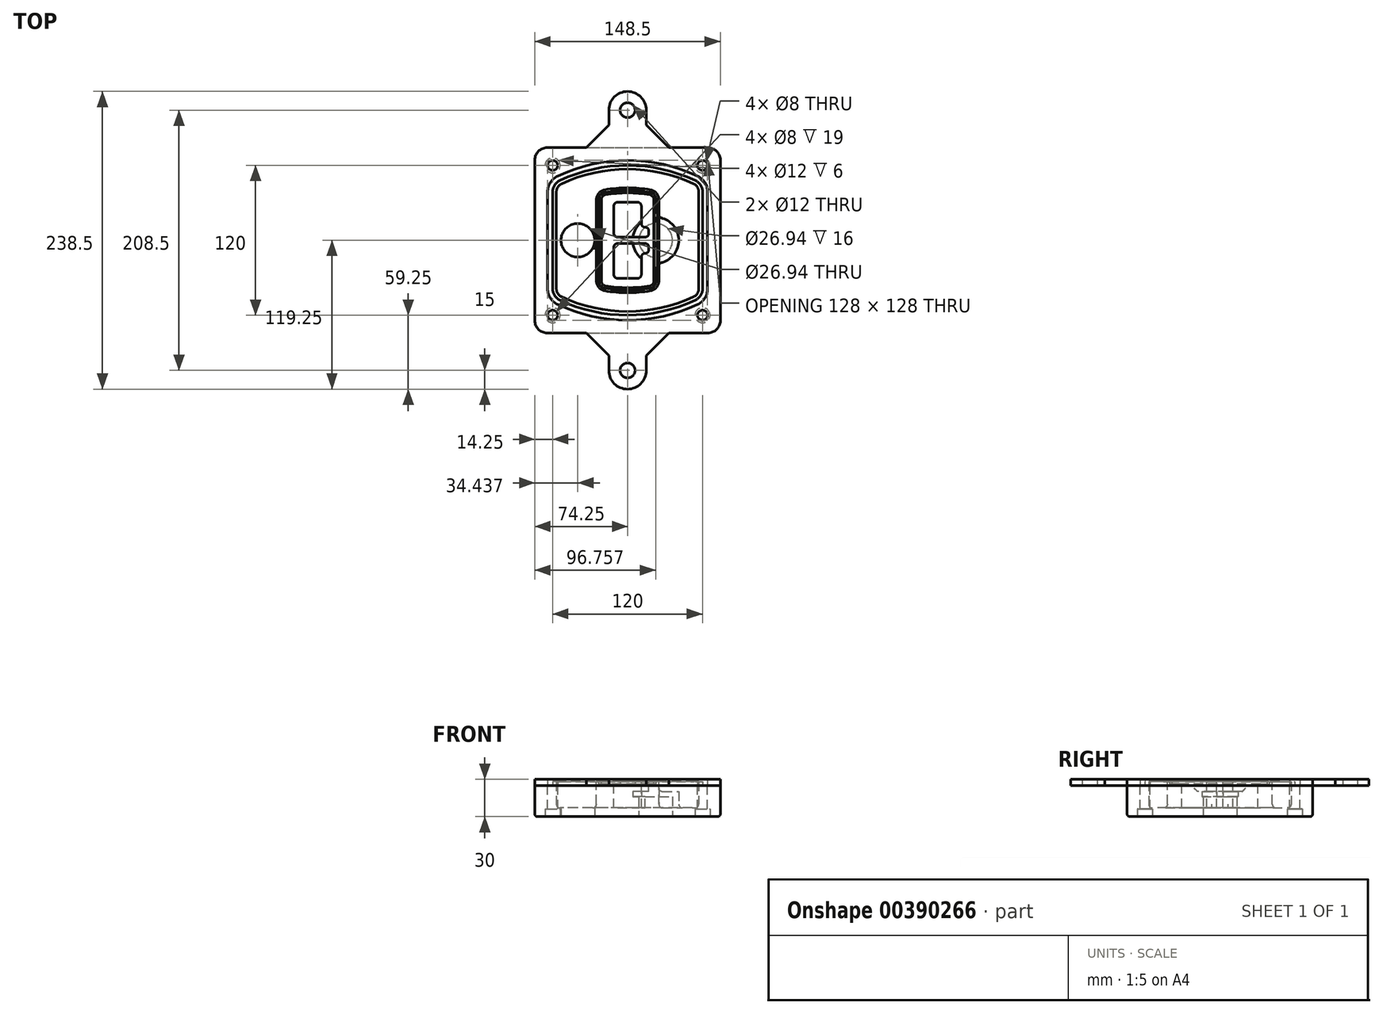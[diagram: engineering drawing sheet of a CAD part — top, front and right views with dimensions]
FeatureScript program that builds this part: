
annotation { "Feature Type Name" : "Feature", "Feature Type Description" : "" }
export const myFeature = defineFeature(function(context is Context, id is Id, definition is map)
    precondition{}
    {
        {
            var Q0;
            Q0=qCreatedBy(makeId("Top.planeOp"),FACE);
            var sketch = newSketch(context, id + "F0", { "sketchPlane" : qUnion([Q0])});
            skPoint(sketch, "E0.rect.middle", {"position": v(0, 0) * mm});
            skLineSegment(sketch, "E1.bottom", {"start": v(-64.25, -74.25) * mm, "end": v(64.25, -74.25) * mm});
            skLineSegment(sketch, "E1.top", {"start": v(-64.25, 74.25) * mm, "end": v(64.25, 74.25) * mm});
            skLineSegment(sketch, "E1.left", {"start": v(-74.25, -64.25) * mm, "end": v(-74.25, 64.25) * mm});
            skLineSegment(sketch, "E1.right", {"start": v(74.25, -64.25) * mm, "end": v(74.25, 64.25) * mm});
            skLineSegment(sketch, "E2", {"start": v(-74.25, 74.25) * mm, "end": v(74.25, -74.25) * mm, "construction": true});
            skLineSegment(sketch, "E3", {"start": v(74.25, 74.25) * mm, "end": v(-74.25, -74.25) * mm, "construction": true});
            skCircle(sketch, "E4", {"center": v(-60, 60) * mm, "radius": 4 * mm});
            skCircle(sketch, "E5", {"center": v(60, 60) * mm, "radius": 4 * mm});
            skCircle(sketch, "E6", {"center": v(60, -60) * mm, "radius": 4 * mm});
            skCircle(sketch, "E7", {"center": v(-60, -60) * mm, "radius": 4 * mm});
            skLineSegment(sketch, "E8", {"start": v(-60, 60) * mm, "end": v(60, 60) * mm, "construction": true});
            skLineSegment(sketch, "E9", {"start": v(60, 60) * mm, "end": v(60, -60) * mm, "construction": true});
            skLineSegment(sketch, "E10", {"start": v(60, -60) * mm, "end": v(-60, -60) * mm, "construction": true});
            skLineSegment(sketch, "E11", {"start": v(-60, -60) * mm, "end": v(-60, 60) * mm, "construction": true});
            skLineSegment(sketch, "E12", {"start": v(-60, 38.83) * mm, "end": v(-60, -38.83) * mm});
            skLineSegment(sketch, "E13", {"start": v(60, 38.83) * mm, "end": v(60, -38.83) * mm});
            skArc(sketch, "E14", {"start": v(54.26, 47.88) * mm, "mid": v(0, 60) * mm, "end": v(-54.26, 47.88) * mm});
            skArc(sketch, "E15", {"start": v(-54.26, -47.88) * mm, "mid": v(0, -60) * mm, "end": v(54.26, -47.88) * mm});
            skLineSegment(sketch, "E16", {"start": v(-60, 0) * mm, "end": v(60, 0) * mm, "construction": true});
            skPoint(sketch, "E17.visualSharp", {"position": v(-60, -45) * mm});
            skArc(sketch, "E17.filletArc", {"start": v(-60, -38.83) * mm, "mid": v(-58.44, -44.2) * mm, "end": v(-54.26, -47.88) * mm});
            skPoint(sketch, "E18.visualSharp", {"position": v(-60, 45) * mm});
            skArc(sketch, "E18.filletArc", {"start": v(-54.26, 47.88) * mm, "mid": v(-58.44, 44.2) * mm, "end": v(-60, 38.83) * mm});
            skPoint(sketch, "E19.visualSharp", {"position": v(60, 45) * mm});
            skArc(sketch, "E19.filletArc", {"start": v(60, 38.83) * mm, "mid": v(58.44, 44.2) * mm, "end": v(54.26, 47.88) * mm});
            skPoint(sketch, "E20.visualSharp", {"position": v(60, -45) * mm});
            skArc(sketch, "E20.filletArc", {"start": v(54.26, -47.88) * mm, "mid": v(58.44, -44.2) * mm, "end": v(60, -38.83) * mm});
            skPoint(sketch, "E21.visualSharp", {"position": v(-74.25, 74.25) * mm});
            skArc(sketch, "E21.filletArc", {"start": v(-64.25, 74.25) * mm, "mid": v(-71.32, 71.32) * mm, "end": v(-74.25, 64.25) * mm});
            skPoint(sketch, "E22.visualSharp", {"position": v(74.25, 74.25) * mm});
            skArc(sketch, "E22.filletArc", {"start": v(74.25, 64.25) * mm, "mid": v(71.32, 71.32) * mm, "end": v(64.25, 74.25) * mm});
            skPoint(sketch, "E23.visualSharp", {"position": v(74.25, -74.25) * mm});
            skArc(sketch, "E23.filletArc", {"start": v(64.25, -74.25) * mm, "mid": v(71.32, -71.32) * mm, "end": v(74.25, -64.25) * mm});
            skPoint(sketch, "E24.visualSharp", {"position": v(-74.25, -74.25) * mm});
            skArc(sketch, "E24.filletArc", {"start": v(-74.25, -64.25) * mm, "mid": v(-71.32, -71.32) * mm, "end": v(-64.25, -74.25) * mm});
            skArc(sketch, "E25.0", {"start": v(57, 38.83) * mm, "mid": v(55.9, 42.58) * mm, "end": v(52.98, 45.17) * mm});
            skLineSegment(sketch, "E25.1", {"start": v(57, 38.83) * mm, "end": v(57, -38.83) * mm});
            skArc(sketch, "E25.2", {"start": v(52.98, -45.17) * mm, "mid": v(55.9, -42.58) * mm, "end": v(57, -38.83) * mm});
            skArc(sketch, "E25.3", {"start": v(-52.98, -45.17) * mm, "mid": v(0, -57) * mm, "end": v(52.98, -45.17) * mm});
            skArc(sketch, "E25.4", {"start": v(-57, -38.83) * mm, "mid": v(-55.9, -42.58) * mm, "end": v(-52.98, -45.17) * mm});
            skArc(sketch, "E25.5", {"start": v(52.98, 45.17) * mm, "mid": v(0, 57) * mm, "end": v(-52.98, 45.17) * mm});
            skLineSegment(sketch, "E25.6", {"start": v(-57, 38.83) * mm, "end": v(-57, -38.83) * mm});
            skArc(sketch, "E25.7", {"start": v(-52.98, 45.17) * mm, "mid": v(-55.9, 42.58) * mm, "end": v(-57, 38.83) * mm});
            skArc(sketch, "E26.0", {"start": v(-55.96, 51.5) * mm, "mid": v(-61.82, 46.33) * mm, "end": v(-64, 38.83) * mm});
            skArc(sketch, "E26.1", {"start": v(55.96, 51.5) * mm, "mid": v(0, 64) * mm, "end": v(-55.96, 51.5) * mm});
            skArc(sketch, "E26.2", {"start": v(64, 38.83) * mm, "mid": v(61.82, 46.33) * mm, "end": v(55.96, 51.5) * mm});
            skLineSegment(sketch, "E26.3", {"start": v(64, 38.83) * mm, "end": v(64, -38.83) * mm});
            skArc(sketch, "E26.4", {"start": v(55.96, -51.5) * mm, "mid": v(61.82, -46.33) * mm, "end": v(64, -38.83) * mm});
            skLineSegment(sketch, "E26.5", {"start": v(-64, 38.83) * mm, "end": v(-64, -38.83) * mm});
            skArc(sketch, "E26.6", {"start": v(-55.96, -51.5) * mm, "mid": v(0, -64) * mm, "end": v(55.96, -51.5) * mm});
            skArc(sketch, "E26.7", {"start": v(-64, -38.83) * mm, "mid": v(-61.82, -46.33) * mm, "end": v(-55.96, -51.5) * mm});
            skCircle(sketch, "E27", {"center": v(0, 104.25) * mm, "radius": 6 * mm});
            skArc(sketch, "E28", {"start": v(15, 104.25) * mm, "mid": v(0, 119.25) * mm, "end": v(-15, 104.25) * mm});
            skLineSegment(sketch, "E29", {"start": v(-15, 104.25) * mm, "end": v(-15, 92.25) * mm});
            skLineSegment(sketch, "E30", {"start": v(15, 104.25) * mm, "end": v(15, 92.25) * mm});
            skLineSegment(sketch, "E31", {"start": v(15, 92.25) * mm, "end": v(33, 74.25) * mm});
            skLineSegment(sketch, "E32", {"start": v(-15, 92.25) * mm, "end": v(-33, 74.25) * mm});
            skLineSegment(sketch, "E33.MirrorCS", {"start": v(-15, -92.25) * mm, "end": v(-33, -74.25) * mm});
            skLineSegment(sketch, "E34.MirrorCS", {"start": v(-15, -104.25) * mm, "end": v(-15, -92.25) * mm});
            skArc(sketch, "E35.MirrorCS", {"start": v(15, -104.25) * mm, "mid": v(0, -119.25) * mm, "end": v(-15, -104.25) * mm});
            skCircle(sketch, "E36.MirrorC", {"center": v(0, -104.25) * mm, "radius": 6 * mm});
            skLineSegment(sketch, "E37.MirrorCS", {"start": v(15, -104.25) * mm, "end": v(15, -92.25) * mm});
            skLineSegment(sketch, "E38.MirrorCS", {"start": v(15, -92.25) * mm, "end": v(33, -74.25) * mm});
            skSolve(sketch);
        }
        {
            var Q0;
            Q0=makeQuery(id+"F0.imprint","IMPRINT",FACE,{"disambiguationData":[TD([[makeQuery(id+"F0.imprint","IMPRINT",EDGE,{"derivedFrom":sQuery(id+"F0.wireOp",EDGE,"E1.bottom")}),1.0]])]});
            var Q1;
            Q1=makeQuery(id+"F0.imprint","IMPRINT",FACE,{"disambiguationData":[TD([[makeQuery(id+"F0.imprint","IMPRINT",EDGE,{"derivedFrom":sQuery(id+"F0.wireOp",EDGE,"E12")}),1.0]])]});
            var Q2;
            Q2=makeQuery(id+"F0.imprint","IMPRINT",FACE,{"disambiguationData":[TD([[makeQuery(id+"F0.imprint","IMPRINT",EDGE,{"derivedFrom":sQuery(id+"F0.wireOp",EDGE,"E25.0")}),1.0]])]});
            var Q3;
            Q3=makeQuery(id+"F0.imprint","IMPRINT",FACE,{"disambiguationData":[TD([[makeQuery(id+"F0.imprint","IMPRINT",EDGE,{"derivedFrom":sQuery(id+"F0.wireOp",EDGE,"E12")}),-1.0]])]});
            extrude(context, id + "F1", {"entities" : qUnion([Q0, Q1, Q2, Q3]), "oppositeDirection" : true, "depth" : 25 * mm});
        }
        {
            var Q0;
            Q0=makeQuery(id+"F0.imprint","IMPRINT",FACE,{"disambiguationData":[TD([[makeQuery(id+"F0.imprint","IMPRINT",EDGE,{"derivedFrom":sQuery(id+"F0.wireOp",EDGE,"E12")}),1.0]])]});
            extrude(context, id + "F2", {"entities" : qUnion([Q0]), "operationType" : NewBodyOperationType.ADD, "depth" : 3 * mm});
        }
        {
            var Q0;
            Q0=makeQuery(id+"F0.imprint","IMPRINT",FACE,{"disambiguationData":[TD([[makeQuery(id+"F0.imprint","IMPRINT",EDGE,{"derivedFrom":sQuery(id+"F0.wireOp",EDGE,"E25.0")}),1.0]])]});
            extrude(context, id + "F3", {"entities" : qUnion([Q0]), "operationType" : NewBodyOperationType.REMOVE, "oppositeDirection" : true, "depth" : 18 * mm});
        }
        {
            var Q0;
            Q0=makeQuery(id+"F2.opExtrude","CAP_FACE",FACE,{"disambiguationData":[OSD([sQuery(id+"F0.wireOp",EDGE,"E12"),sQuery(id+"F0.wireOp",EDGE,"E13"),sQuery(id+"F0.wireOp",EDGE,"E14"),sQuery(id+"F0.wireOp",EDGE,"E15"),sQuery(id+"F0.wireOp",EDGE,"E17.filletArc"),sQuery(id+"F0.wireOp",EDGE,"E18.filletArc"),sQuery(id+"F0.wireOp",EDGE,"E19.filletArc"),sQuery(id+"F0.wireOp",EDGE,"E20.filletArc"),sQuery(id+"F0.wireOp",EDGE,"E25.0"),sQuery(id+"F0.wireOp",EDGE,"E25.1"),sQuery(id+"F0.wireOp",EDGE,"E25.2"),sQuery(id+"F0.wireOp",EDGE,"E25.3"),sQuery(id+"F0.wireOp",EDGE,"E25.4"),sQuery(id+"F0.wireOp",EDGE,"E25.5"),sQuery(id+"F0.wireOp",EDGE,"E25.6"),sQuery(id+"F0.wireOp",EDGE,"E25.7")])],"isStart":false});
            var sketch = newSketch(context, id + "F4", { "sketchPlane" : qUnion([Q0])});
            skArc(sketch, "E39.0", {"start": v(-18.34, -40.45) * mm, "mid": v(0, -42) * mm, "end": v(18.34, -40.45) * mm});
            skArc(sketch, "E40.0", {"start": v(18.34, 40.45) * mm, "mid": v(0, 42) * mm, "end": v(-18.34, 40.45) * mm});
            skLineSegment(sketch, "E41", {"start": v(-25, 32.57) * mm, "end": v(-25, -32.57) * mm});
            skLineSegment(sketch, "E42", {"start": v(25, 32.57) * mm, "end": v(25, -32.57) * mm});
            skLineSegment(sketch, "E43", {"start": v(-25, 39.1) * mm, "end": v(25, 39.1) * mm, "construction": true});
            skLineSegment(sketch, "E44", {"start": v(-25, -39.1) * mm, "end": v(25, -39.1) * mm, "construction": true});
            skPoint(sketch, "E45.visualSharp", {"position": v(-25, 39.1) * mm});
            skArc(sketch, "E45.filletArc", {"start": v(-18.34, 40.45) * mm, "mid": v(-23.11, 37.73) * mm, "end": v(-25, 32.57) * mm});
            skPoint(sketch, "E46.visualSharp", {"position": v(25, 39.1) * mm});
            skArc(sketch, "E46.filletArc", {"start": v(25, 32.57) * mm, "mid": v(23.11, 37.73) * mm, "end": v(18.34, 40.45) * mm});
            skPoint(sketch, "E47.visualSharp", {"position": v(25, -39.1) * mm});
            skArc(sketch, "E47.filletArc", {"start": v(18.34, -40.45) * mm, "mid": v(23.11, -37.73) * mm, "end": v(25, -32.57) * mm});
            skPoint(sketch, "E48.visualSharp", {"position": v(-25, -39.1) * mm});
            skArc(sketch, "E48.filletArc", {"start": v(-25, -32.57) * mm, "mid": v(-23.11, -37.73) * mm, "end": v(-18.34, -40.45) * mm});
            skArc(sketch, "E49.0", {"start": v(52.98, 45.17) * mm, "mid": v(0, 57) * mm, "end": v(-52.98, 45.17) * mm});
            skArc(sketch, "E49.1", {"start": v(-52.98, 45.17) * mm, "mid": v(-55.9, 42.58) * mm, "end": v(-57, 38.83) * mm});
            skLineSegment(sketch, "E49.2", {"start": v(-57, 38.83) * mm, "end": v(-57, -38.83) * mm});
            skArc(sketch, "E49.3", {"start": v(-57, -38.83) * mm, "mid": v(-55.9, -42.58) * mm, "end": v(-52.98, -45.17) * mm});
            skArc(sketch, "E49.4", {"start": v(-52.98, -45.17) * mm, "mid": v(0, -57) * mm, "end": v(52.98, -45.17) * mm});
            skArc(sketch, "E49.5", {"start": v(52.98, -45.17) * mm, "mid": v(55.9, -42.58) * mm, "end": v(57, -38.83) * mm});
            skLineSegment(sketch, "E49.6", {"start": v(57, 38.83) * mm, "end": v(57, -38.83) * mm});
            skArc(sketch, "E49.7", {"start": v(57, 38.83) * mm, "mid": v(55.9, 42.58) * mm, "end": v(52.98, 45.17) * mm});
            skLineSegment(sketch, "E50.0", {"start": v(23, 32.57) * mm, "end": v(23, -32.57) * mm});
            skArc(sketch, "E50.1", {"start": v(18, -38.48) * mm, "mid": v(21.58, -36.44) * mm, "end": v(23, -32.57) * mm});
            skArc(sketch, "E50.2", {"start": v(-18, -38.48) * mm, "mid": v(0, -40) * mm, "end": v(18, -38.48) * mm});
            skArc(sketch, "E50.3", {"start": v(-23, -32.57) * mm, "mid": v(-21.58, -36.44) * mm, "end": v(-18, -38.48) * mm});
            skLineSegment(sketch, "E50.4", {"start": v(-23, 32.57) * mm, "end": v(-23, -32.57) * mm});
            skArc(sketch, "E50.5", {"start": v(23, 32.57) * mm, "mid": v(21.58, 36.44) * mm, "end": v(18, 38.48) * mm});
            skArc(sketch, "E50.6", {"start": v(-18, 38.48) * mm, "mid": v(-21.58, 36.44) * mm, "end": v(-23, 32.57) * mm});
            skArc(sketch, "E50.7", {"start": v(18, 38.48) * mm, "mid": v(0, 40) * mm, "end": v(-18, 38.48) * mm});
            skArc(sketch, "E51.0", {"start": v(21, 32.57) * mm, "mid": v(20.06, 35.15) * mm, "end": v(17.67, 36.5) * mm});
            skLineSegment(sketch, "E51.1", {"start": v(21, 32.57) * mm, "end": v(21, -32.57) * mm});
            skArc(sketch, "E51.2", {"start": v(17.67, -36.5) * mm, "mid": v(20.06, -35.15) * mm, "end": v(21, -32.57) * mm});
            skArc(sketch, "E51.3", {"start": v(-17.67, -36.5) * mm, "mid": v(0, -38) * mm, "end": v(17.67, -36.5) * mm});
            skArc(sketch, "E51.4", {"start": v(-21, -32.57) * mm, "mid": v(-20.06, -35.15) * mm, "end": v(-17.67, -36.5) * mm});
            skArc(sketch, "E51.5", {"start": v(17.67, 36.5) * mm, "mid": v(0, 38) * mm, "end": v(-17.67, 36.5) * mm});
            skLineSegment(sketch, "E51.6", {"start": v(-21, 32.57) * mm, "end": v(-21, -32.57) * mm});
            skArc(sketch, "E51.7", {"start": v(-17.67, 36.5) * mm, "mid": v(-20.06, 35.15) * mm, "end": v(-21, 32.57) * mm});
            skLineSegment(sketch, "E52", {"start": v(-25, 0) * mm, "end": v(25, 0) * mm, "construction": true});
            skLineSegment(sketch, "E53", {"start": v(-11, 5.5) * mm, "end": v(-11, 27.5) * mm});
            skLineSegment(sketch, "E54", {"start": v(-8, 30.5) * mm, "end": v(8, 30.5) * mm});
            skLineSegment(sketch, "E55", {"start": v(11, 27.5) * mm, "end": v(11, 13.5) * mm});
            skLineSegment(sketch, "E56", {"start": v(14, 10.5) * mm, "end": v(14, 10.5) * mm});
            skLineSegment(sketch, "E57", {"start": v(17, 7.5) * mm, "end": v(17, 5.5) * mm});
            skLineSegment(sketch, "E58", {"start": v(14, 2.5) * mm, "end": v(-8, 2.5) * mm});
            skPoint(sketch, "E59.visualSharp", {"position": v(-11, 30.5) * mm});
            skArc(sketch, "E59.filletArc", {"start": v(-8, 30.5) * mm, "mid": v(-10.12, 29.62) * mm, "end": v(-11, 27.5) * mm});
            skPoint(sketch, "E60.visualSharp", {"position": v(11, 30.5) * mm});
            skArc(sketch, "E60.filletArc", {"start": v(11, 27.5) * mm, "mid": v(10.12, 29.62) * mm, "end": v(8, 30.5) * mm});
            skPoint(sketch, "E61.visualSharp", {"position": v(11, 10.5) * mm});
            skArc(sketch, "E61.filletArc", {"start": v(11, 13.5) * mm, "mid": v(11.88, 11.38) * mm, "end": v(14, 10.5) * mm});
            skPoint(sketch, "E62.visualSharp", {"position": v(17, 10.5) * mm});
            skArc(sketch, "E62.filletArc", {"start": v(17, 7.5) * mm, "mid": v(16.12, 9.62) * mm, "end": v(14, 10.5) * mm});
            skPoint(sketch, "E63.visualSharp", {"position": v(17, 2.5) * mm});
            skArc(sketch, "E63.filletArc", {"start": v(14, 2.5) * mm, "mid": v(16.12, 3.38) * mm, "end": v(17, 5.5) * mm});
            skPoint(sketch, "E64.visualSharp", {"position": v(-11, 2.5) * mm});
            skArc(sketch, "E64.filletArc", {"start": v(-11, 5.5) * mm, "mid": v(-10.12, 3.38) * mm, "end": v(-8, 2.5) * mm});
            skLineSegment(sketch, "E65.0.MirrorCS", {"start": v(14, -2.5) * mm, "end": v(-8, -2.5) * mm});
            skArc(sketch, "E66.0.MirrorCS", {"start": v(-11, -5.5) * mm, "mid": v(-10.12, -3.38) * mm, "end": v(-8, -2.5) * mm});
            skLineSegment(sketch, "E67.0.MirrorCS", {"start": v(-11, -5.5) * mm, "end": v(-11, -27.5) * mm});
            skArc(sketch, "E68.0.MirrorCS", {"start": v(-8, -30.5) * mm, "mid": v(-10.12, -29.62) * mm, "end": v(-11, -27.5) * mm});
            skLineSegment(sketch, "E69.0.MirrorCS", {"start": v(-8, -30.5) * mm, "end": v(8, -30.5) * mm});
            skArc(sketch, "E70.0.MirrorCS", {"start": v(11, -27.5) * mm, "mid": v(10.12, -29.62) * mm, "end": v(8, -30.5) * mm});
            skLineSegment(sketch, "E71.0.MirrorCS", {"start": v(11, -27.5) * mm, "end": v(11, -13.5) * mm});
            skArc(sketch, "E72.0.MirrorCS", {"start": v(11, -13.5) * mm, "mid": v(11.88, -11.38) * mm, "end": v(14, -10.5) * mm});
            skArc(sketch, "E73.0.MirrorCS", {"start": v(17, -7.5) * mm, "mid": v(16.12, -9.62) * mm, "end": v(14, -10.5) * mm});
            skLineSegment(sketch, "E74.0.MirrorCS", {"start": v(17, -7.5) * mm, "end": v(17, -5.5) * mm});
            skArc(sketch, "E75.0.MirrorCS", {"start": v(14, -2.5) * mm, "mid": v(16.12, -3.38) * mm, "end": v(17, -5.5) * mm});
            skSolve(sketch);
        }
        {
            var Q0;
            Q0=makeQuery(id+"F4.imprint","IMPRINT",FACE,{"disambiguationData":[TD([[makeQuery(id+"F4.imprint","IMPRINT",EDGE,{"derivedFrom":sQuery(id+"F4.wireOp",EDGE,"E39.0")}),1.0]])]});
            var Q1;
            Q1=makeQuery(id+"F4.imprint","IMPRINT",FACE,{"disambiguationData":[TD([[makeQuery(id+"F4.imprint","IMPRINT",EDGE,{"derivedFrom":sQuery(id+"F4.wireOp",EDGE,"E50.0")}),-1.0]])]});
            var Q2;
            Q2=makeQuery(id+"F4.imprint","IMPRINT",FACE,{"disambiguationData":[TD([[makeQuery(id+"F4.imprint","IMPRINT",EDGE,{"derivedFrom":sQuery(id+"F4.wireOp",EDGE,"E51.0")}),1.0]])]});
            extrude(context, id + "F5", {"entities" : qUnion([Q0, Q1, Q2]), "operationType" : NewBodyOperationType.ADD, "endBound" : BoundingType.UP_TO_NEXT, "oppositeDirection" : true, "depth" : 25 * mm});
        }
        {
            var Q0;
            Q0=makeQuery(id+"F4.imprint","IMPRINT",FACE,{"disambiguationData":[TD([[makeQuery(id+"F4.imprint","IMPRINT",EDGE,{"derivedFrom":sQuery(id+"F4.wireOp",EDGE,"E50.0")}),-1.0]])]});
            extrude(context, id + "F6", {"entities" : qUnion([Q0]), "operationType" : NewBodyOperationType.REMOVE, "oppositeDirection" : true, "depth" : 2 * mm});
        }
        {
            var Q0;
            Q0=makeQuery(id+"F1.opExtrude","CAP_FACE",FACE,{"disambiguationData":[OSD([sQuery(id+"F0.wireOp",EDGE,"E1.bottom"),sQuery(id+"F0.wireOp",EDGE,"E1.top"),sQuery(id+"F0.wireOp",EDGE,"E1.left"),sQuery(id+"F0.wireOp",EDGE,"E1.right"),sQuery(id+"F0.wireOp",EDGE,"E4"),sQuery(id+"F0.wireOp",EDGE,"E5"),sQuery(id+"F0.wireOp",EDGE,"E6"),sQuery(id+"F0.wireOp",EDGE,"E7"),sQuery(id+"F0.wireOp",EDGE,"E21.filletArc"),sQuery(id+"F0.wireOp",EDGE,"E22.filletArc"),sQuery(id+"F0.wireOp",EDGE,"E23.filletArc"),sQuery(id+"F0.wireOp",EDGE,"E24.filletArc")])],"isStart":false});
            var sketch = newSketch(context, id + "F7", { "sketchPlane" : qUnion([Q0])});
            skCircle(sketch, "E76", {"center": v(22.5, 0) * mm, "radius": 13.47 * mm});
            skCircle(sketch, "E77", {"center": v(-39.81, 0) * mm, "radius": 13.47 * mm});
            skLineSegment(sketch, "E78", {"start": v(74.25, 0) * mm, "end": v(-74.25, 0) * mm});
            skCircle(sketch, "E79", {"center": v(22.5, 0) * mm, "radius": 18.47 * mm});
            skCircle(sketch, "E80", {"center": v(60, -60) * mm, "radius": 6 * mm});
            skCircle(sketch, "E81", {"center": v(-60, -60) * mm, "radius": 6 * mm});
            skCircle(sketch, "E82", {"center": v(-60, 60) * mm, "radius": 6 * mm});
            skCircle(sketch, "E83", {"center": v(60, 60) * mm, "radius": 6 * mm});
            skSolve(sketch);
        }
        {
            var Q0;
            {var subQ1=sQuery(id+"F7.wireOp",EDGE,"E78");var subQ4=sQuery(id+"F7.wireOp",EDGE,"E76");var subQ6=makeQuery(id+"F7.imprint","INTERSECT",VERTEX,{"disambiguationData":[OD(0.0)],"derivedFrom":[subQ4,subQ1]});Q0=makeQuery(id+"F7.imprint","IMPRINT",FACE,{"disambiguationData":[TD([[makeQuery(id+"F7.imprint","IMPRINT",EDGE,{"disambiguationData":[TD([[subQ6,-1.0]])],"derivedFrom":subQ4}),-1.0]])]});}
            var Q1;
            {var subQ0=sQuery(id+"F7.wireOp",EDGE,"E78");var subQ1=sQuery(id+"F7.wireOp",EDGE,"E76");var subQ3=makeQuery(id+"F7.imprint","INTERSECT",VERTEX,{"disambiguationData":[OD(0.0)],"derivedFrom":[subQ1,subQ0]});Q1=makeQuery(id+"F7.imprint","IMPRINT",FACE,{"disambiguationData":[TD([[makeQuery(id+"F7.imprint","IMPRINT",EDGE,{"disambiguationData":[TD([[subQ3,-1.0]])],"derivedFrom":subQ1}),1.0]])]});}
            var Q2;
            {var subQ0=sQuery(id+"F7.wireOp",EDGE,"E78");var subQ1=sQuery(id+"F7.wireOp",EDGE,"E76");var subQ3=makeQuery(id+"F7.imprint","INTERSECT",VERTEX,{"disambiguationData":[OD(0.0)],"derivedFrom":[subQ1,subQ0]});Q2=makeQuery(id+"F7.imprint","IMPRINT",FACE,{"disambiguationData":[TD([[makeQuery(id+"F7.imprint","IMPRINT",EDGE,{"disambiguationData":[TD([[subQ3,1.0]])],"derivedFrom":subQ1}),1.0]])]});}
            var Q3;
            {var subQ1=sQuery(id+"F7.wireOp",EDGE,"E78");var subQ4=sQuery(id+"F7.wireOp",EDGE,"E76");var subQ6=makeQuery(id+"F7.imprint","INTERSECT",VERTEX,{"disambiguationData":[OD(0.0)],"derivedFrom":[subQ4,subQ1]});Q3=makeQuery(id+"F7.imprint","IMPRINT",FACE,{"disambiguationData":[TD([[makeQuery(id+"F7.imprint","IMPRINT",EDGE,{"disambiguationData":[TD([[subQ6,1.0]])],"derivedFrom":subQ4}),-1.0]])]});}
            extrude(context, id + "F8", {"entities" : qUnion([Q0, Q1, Q2, Q3]), "operationType" : NewBodyOperationType.ADD, "oppositeDirection" : true, "depth" : 20 * mm});
        }
        {
            var Q0;
            {var subQ0=sQuery(id+"F7.wireOp",EDGE,"E78");var subQ1=sQuery(id+"F7.wireOp",EDGE,"E76");var subQ3=makeQuery(id+"F7.imprint","INTERSECT",VERTEX,{"disambiguationData":[OD(0.0)],"derivedFrom":[subQ1,subQ0]});Q0=makeQuery(id+"F7.imprint","IMPRINT",FACE,{"disambiguationData":[TD([[makeQuery(id+"F7.imprint","IMPRINT",EDGE,{"disambiguationData":[TD([[subQ3,-1.0]])],"derivedFrom":subQ1}),1.0]])]});}
            var Q1;
            {var subQ0=sQuery(id+"F7.wireOp",EDGE,"E78");var subQ1=sQuery(id+"F7.wireOp",EDGE,"E76");var subQ3=makeQuery(id+"F7.imprint","INTERSECT",VERTEX,{"disambiguationData":[OD(0.0)],"derivedFrom":[subQ1,subQ0]});Q1=makeQuery(id+"F7.imprint","IMPRINT",FACE,{"disambiguationData":[TD([[makeQuery(id+"F7.imprint","IMPRINT",EDGE,{"disambiguationData":[TD([[subQ3,1.0]])],"derivedFrom":subQ1}),1.0]])]});}
            extrude(context, id + "F9", {"entities" : qUnion([Q0, Q1]), "operationType" : NewBodyOperationType.REMOVE, "oppositeDirection" : true, "depth" : 16 * mm});
        }
        {
            var Q0;
            {var subQ0=sQuery(id+"F7.wireOp",EDGE,"E78");var subQ1=sQuery(id+"F7.wireOp",EDGE,"E77");var subQ3=makeQuery(id+"F7.imprint","INTERSECT",VERTEX,{"disambiguationData":[OD(0.0)],"derivedFrom":[subQ1,subQ0]});Q0=makeQuery(id+"F7.imprint","IMPRINT",FACE,{"disambiguationData":[TD([[makeQuery(id+"F7.imprint","IMPRINT",EDGE,{"disambiguationData":[TD([[subQ3,-1.0]])],"derivedFrom":subQ1}),1.0]])]});}
            var Q1;
            {var subQ0=sQuery(id+"F7.wireOp",EDGE,"E78");var subQ1=sQuery(id+"F7.wireOp",EDGE,"E77");var subQ3=makeQuery(id+"F7.imprint","INTERSECT",VERTEX,{"disambiguationData":[OD(0.0)],"derivedFrom":[subQ1,subQ0]});Q1=makeQuery(id+"F7.imprint","IMPRINT",FACE,{"disambiguationData":[TD([[makeQuery(id+"F7.imprint","IMPRINT",EDGE,{"disambiguationData":[TD([[subQ3,1.0]])],"derivedFrom":subQ1}),1.0]])]});}
            extrude(context, id + "F10", {"entities" : qUnion([Q0, Q1]), "operationType" : NewBodyOperationType.REMOVE, "oppositeDirection" : true, "depth" : 25 * mm});
        }
        {
            var Q0;
            Q0=makeQuery(id+"F7.imprint","IMPRINT",FACE,{"disambiguationData":[TD([[makeQuery(id+"F7.imprint","IMPRINT",EDGE,{"derivedFrom":sQuery(id+"F7.wireOp",EDGE,"E80")}),1.0]])]});
            var Q1;
            Q1=makeQuery(id+"F7.imprint","IMPRINT",FACE,{"disambiguationData":[TD([[makeQuery(id+"F7.imprint","IMPRINT",EDGE,{"derivedFrom":makeQuery(id+"F1.opExtrude","CAP_EDGE",EDGE,{"disambiguationData":[OSD([sQuery(id+"F0.wireOp",EDGE,"E5")])],"isStart":false})}),-1.0]])]});
            var Q2;
            Q2=makeQuery(id+"F7.imprint","IMPRINT",FACE,{"disambiguationData":[TD([[makeQuery(id+"F7.imprint","IMPRINT",EDGE,{"derivedFrom":sQuery(id+"F7.wireOp",EDGE,"E81")}),1.0]])]});
            var Q3;
            Q3=makeQuery(id+"F7.imprint","IMPRINT",FACE,{"disambiguationData":[TD([[makeQuery(id+"F7.imprint","IMPRINT",EDGE,{"derivedFrom":makeQuery(id+"F1.opExtrude","CAP_EDGE",EDGE,{"disambiguationData":[OSD([sQuery(id+"F0.wireOp",EDGE,"E4")])],"isStart":false})}),-1.0]])]});
            var Q4;
            Q4=makeQuery(id+"F7.imprint","IMPRINT",FACE,{"disambiguationData":[TD([[makeQuery(id+"F7.imprint","IMPRINT",EDGE,{"derivedFrom":sQuery(id+"F7.wireOp",EDGE,"E82")}),1.0]])]});
            var Q5;
            Q5=makeQuery(id+"F7.imprint","IMPRINT",FACE,{"disambiguationData":[TD([[makeQuery(id+"F7.imprint","IMPRINT",EDGE,{"derivedFrom":makeQuery(id+"F1.opExtrude","CAP_EDGE",EDGE,{"disambiguationData":[OSD([sQuery(id+"F0.wireOp",EDGE,"E7")])],"isStart":false})}),-1.0]])]});
            var Q6;
            Q6=makeQuery(id+"F7.imprint","IMPRINT",FACE,{"disambiguationData":[TD([[makeQuery(id+"F7.imprint","IMPRINT",EDGE,{"derivedFrom":sQuery(id+"F7.wireOp",EDGE,"E83")}),1.0]])]});
            var Q7;
            Q7=makeQuery(id+"F7.imprint","IMPRINT",FACE,{"disambiguationData":[TD([[makeQuery(id+"F7.imprint","IMPRINT",EDGE,{"derivedFrom":makeQuery(id+"F1.opExtrude","CAP_EDGE",EDGE,{"disambiguationData":[OSD([sQuery(id+"F0.wireOp",EDGE,"E6")])],"isStart":false})}),-1.0]])]});
            extrude(context, id + "F11", {"entities" : qUnion([Q0, Q1, Q2, Q3, Q4, Q5, Q6, Q7]), "operationType" : NewBodyOperationType.REMOVE, "oppositeDirection" : true, "depth" : 6 * mm});
        }
        {
            var Q0;
            Q0=makeQuery(id+"F9.boolean.opBoolean","COPY",FACE,{"derivedFrom":makeQuery(id+"F9.opExtrude","CAP_FACE",FACE,{"disambiguationData":[OSD([sQuery(id+"F7.wireOp",EDGE,"E76")])],"isStart":false})});
            var sketch = newSketch(context, id + "F12", { "sketchPlane" : qUnion([Q0])});
            skArc(sketch, "E84.0", {"start": v(11, 14.45) * mm, "mid": v(6.45, 9.13) * mm, "end": v(4.2, 2.5) * mm});
            skArc(sketch, "E84.1", {"start": v(4.2, -2.5) * mm, "mid": v(6.45, -9.13) * mm, "end": v(11, -14.45) * mm});
            skLineSegment(sketch, "E85", {"start": v(4.2, -2.5) * mm, "end": v(14, -2.5) * mm});
            skLineSegment(sketch, "E86.0", {"start": v(14, 2.5) * mm, "end": v(4.2, 2.5) * mm});
            skArc(sketch, "E86.1", {"start": v(14, 2.5) * mm, "mid": v(16.12, 3.38) * mm, "end": v(17, 5.5) * mm});
            skLineSegment(sketch, "E86.2", {"start": v(17, 7.5) * mm, "end": v(17, 5.5) * mm});
            skArc(sketch, "E86.3", {"start": v(17, 7.5) * mm, "mid": v(16.12, 9.62) * mm, "end": v(14, 10.5) * mm});
            skArc(sketch, "E86.4", {"start": v(11, 13.5) * mm, "mid": v(11.88, 11.38) * mm, "end": v(14, 10.5) * mm});
            skLineSegment(sketch, "E86.5", {"start": v(11, 14.45) * mm, "end": v(11, 13.5) * mm});
            skLineSegment(sketch, "E86.7", {"start": v(14, -2.5) * mm, "end": v(4.2, -2.5) * mm});
            skArc(sketch, "E86.8", {"start": v(14, -2.5) * mm, "mid": v(16.12, -3.38) * mm, "end": v(17, -5.5) * mm});
            skLineSegment(sketch, "E86.9", {"start": v(17, -7.5) * mm, "end": v(17, -5.5) * mm});
            skArc(sketch, "E86.10", {"start": v(17, -7.5) * mm, "mid": v(16.12, -9.62) * mm, "end": v(14, -10.5) * mm});
            skArc(sketch, "E86.11", {"start": v(11, -13.5) * mm, "mid": v(11.88, -11.38) * mm, "end": v(14, -10.5) * mm});
            skLineSegment(sketch, "E86.12", {"start": v(11, -14.45) * mm, "end": v(11, -13.5) * mm});
            skPoint(sketch, "E87.orphan", {"position": v(11, -27.5) * mm});
            skPoint(sketch, "E88.orphan", {"position": v(-8, -2.5) * mm});
            skPoint(sketch, "E89.orphan", {"position": v(-8, 2.5) * mm});
            skPoint(sketch, "E90.orphan", {"position": v(11, 27.5) * mm});
            skSolve(sketch);
        }
        {
            var Q0;
            {var subQ7=sQuery(id+"F12.wireOp",EDGE,"E84.0");var subQ14=sQuery(id+"F12.wireOp",EDGE,"E84.1");var subQ16=sQuery(id+"F12.wireOp",EDGE,"E86.1");var subQ18=sQuery(id+"F12.wireOp",EDGE,"E86.8");Q0=qUnion([makeQuery(id+"F12.imprint","IMPRINT",FACE,{"disambiguationData":[TD([[makeQuery(id+"F12.imprint","IMPRINT",EDGE,{"derivedFrom":subQ7}),1.0]])]}),makeQuery(id+"F12.imprint","IMPRINT",FACE,{"disambiguationData":[TD([[makeQuery(id+"F12.imprint","IMPRINT",EDGE,{"derivedFrom":subQ14}),1.0]])]}),makeQuery(id+"F12.imprint","IMPRINT",FACE,{"disambiguationData":[TD([[makeQuery(id+"F12.imprint","IMPRINT",EDGE,{"derivedFrom":subQ16}),1.0]])]}),makeQuery(id+"F12.imprint","IMPRINT",FACE,{"disambiguationData":[TD([[makeQuery(id+"F12.imprint","IMPRINT",EDGE,{"derivedFrom":subQ18}),-1.0]])]})]);}
            var Q1;
            Q1=makeQuery(id+"F5.boolean.opBoolean","SPLIT",FACE,{"disambiguationData":[TD([makeQuery(id+"F5.opExtrude","SWEPT_FACE",FACE,{"disambiguationData":[OSD([sQuery(id+"F4.wireOp",EDGE,"E53")])]})])],"derivedFrom":makeQuery(id+"F3.boolean.opBoolean","COPY",FACE,{"derivedFrom":makeQuery(id+"F3.opExtrude","CAP_FACE",FACE,{"disambiguationData":[OSD([sQuery(id+"F0.wireOp",EDGE,"E25.0"),sQuery(id+"F0.wireOp",EDGE,"E25.1"),sQuery(id+"F0.wireOp",EDGE,"E25.2"),sQuery(id+"F0.wireOp",EDGE,"E25.3"),sQuery(id+"F0.wireOp",EDGE,"E25.4"),sQuery(id+"F0.wireOp",EDGE,"E25.5"),sQuery(id+"F0.wireOp",EDGE,"E25.6"),sQuery(id+"F0.wireOp",EDGE,"E25.7")])],"isStart":false})})});
            extrude(context, id + "F13", {"entities" : qUnion([Q0]), "operationType" : NewBodyOperationType.REMOVE, "endBound" : BoundingType.UP_TO_SURFACE, "endBoundEntityFace" : qUnion([Q1]), "depth" : 25 * mm});
        }
        {
            var Q0;
            Q0=makeQuery(id+"F3.boolean.opBoolean","COPY",EDGE,{"derivedFrom":makeQuery(id+"F3.opExtrude","CAP_EDGE",EDGE,{"disambiguationData":[OSD([sQuery(id+"F0.wireOp",EDGE,"E25.6")])],"isStart":false})});
            var Q1;
            Q1=makeQuery(id+"F8.boolean.opBoolean","INTERSECT",EDGE,{"derivedFrom":[makeQuery(id+"F5.opExtrude","SWEPT_FACE",FACE,{"disambiguationData":[OSD([sQuery(id+"F4.wireOp",EDGE,"E42")])]}),makeQuery(id+"F8.opExtrude","CAP_FACE",FACE,{"disambiguationData":[OSD([sQuery(id+"F7.wireOp",EDGE,"E79")])],"isStart":false})]});
            var Q2;
            Q2=makeQuery(id+"F8.boolean.opBoolean","INTERSECT",EDGE,{"disambiguationData":[OD(1.0)],"derivedFrom":[makeQuery(id+"F5.opExtrude","SWEPT_FACE",FACE,{"disambiguationData":[OSD([sQuery(id+"F4.wireOp",EDGE,"E42")])]}),makeQuery(id+"F8.opExtrude","SWEPT_FACE",FACE,{"disambiguationData":[OSD([sQuery(id+"F7.wireOp",EDGE,"E79")])]})]});
            var Q3;
            {var subQ0=sQuery(id+"F4.wireOp",EDGE,"E42");Q3=makeQuery(id+"F8.boolean.opBoolean","SPLIT",EDGE,{"disambiguationData":[TD([makeQuery(id+"F5.opExtrude","SWEPT_FACE",FACE,{"disambiguationData":[OSD([sQuery(id+"F4.wireOp",EDGE,"E47.filletArc")])]})])],"derivedFrom":makeQuery(id+"F5.opExtrude","CAP_EDGE",EDGE,{"disambiguationData":[OSD([subQ0])],"isStart":false})});}
            var Q4;
            {var subQ0=sQuery(id+"F0.wireOp",EDGE,"E25.7");var subQ1=sQuery(id+"F0.wireOp",EDGE,"E25.1");var subQ2=sQuery(id+"F0.wireOp",EDGE,"E25.6");var subQ3=sQuery(id+"F0.wireOp",EDGE,"E25.5");var subQ4=sQuery(id+"F0.wireOp",EDGE,"E25.4");var subQ5=sQuery(id+"F0.wireOp",EDGE,"E25.0");var subQ6=sQuery(id+"F0.wireOp",EDGE,"E25.2");var subQ7=sQuery(id+"F0.wireOp",EDGE,"E25.3");Q4=makeQuery(id+"F8.boolean.opBoolean","INTERSECT",EDGE,{"derivedFrom":[makeQuery(id+"F5.boolean.opBoolean","SPLIT",FACE,{"disambiguationData":[TD([makeQuery(id+"F2.opExtrude","SWEPT_FACE",FACE,{"disambiguationData":[OSD([subQ5])]})])],"derivedFrom":makeQuery(id+"F3.boolean.opBoolean","COPY",FACE,{"derivedFrom":makeQuery(id+"F3.opExtrude","CAP_FACE",FACE,{"disambiguationData":[OSD([subQ5,subQ1,subQ6,subQ7,subQ4,subQ3,subQ2,subQ0])],"isStart":false})})}),makeQuery(id+"F8.opExtrude","SWEPT_FACE",FACE,{"disambiguationData":[OSD([sQuery(id+"F7.wireOp",EDGE,"E79")])]})]});}
            var Q5;
            Q5=makeQuery(id+"F8.boolean.opBoolean","INTERSECT",EDGE,{"disambiguationData":[OD(0.0)],"derivedFrom":[makeQuery(id+"F5.opExtrude","SWEPT_FACE",FACE,{"disambiguationData":[OSD([sQuery(id+"F4.wireOp",EDGE,"E42")])]}),makeQuery(id+"F8.opExtrude","SWEPT_FACE",FACE,{"disambiguationData":[OSD([sQuery(id+"F7.wireOp",EDGE,"E79")])]})]});
            fillet(context, id + "F14", {"entities" : qUnion([Q0, Q1, Q2, Q3, Q4, Q5]), "radius" : 3 * mm, "tangentPropagation" : true, "allowEdgeOverflow" : false});
        }
        {
            var Q0;
            Q0=makeQuery(id+"F1.opExtrude","CAP_EDGE",EDGE,{"disambiguationData":[OSD([sQuery(id+"F0.wireOp",EDGE,"E1.bottom")])],"isStart":false});
            fillet(context, id + "F15", {"entities" : qUnion([Q0]), "radius" : 2 * mm, "tangentPropagation" : true, "allowEdgeOverflow" : false});
        }
        {
            var Q0;
            Q0 = qSketchRegion(id + "F0", true);
            extrude(context, id + "F16", {"entities" : qUnion([Q0]), "depth" : 5 * mm});
        }
    });
